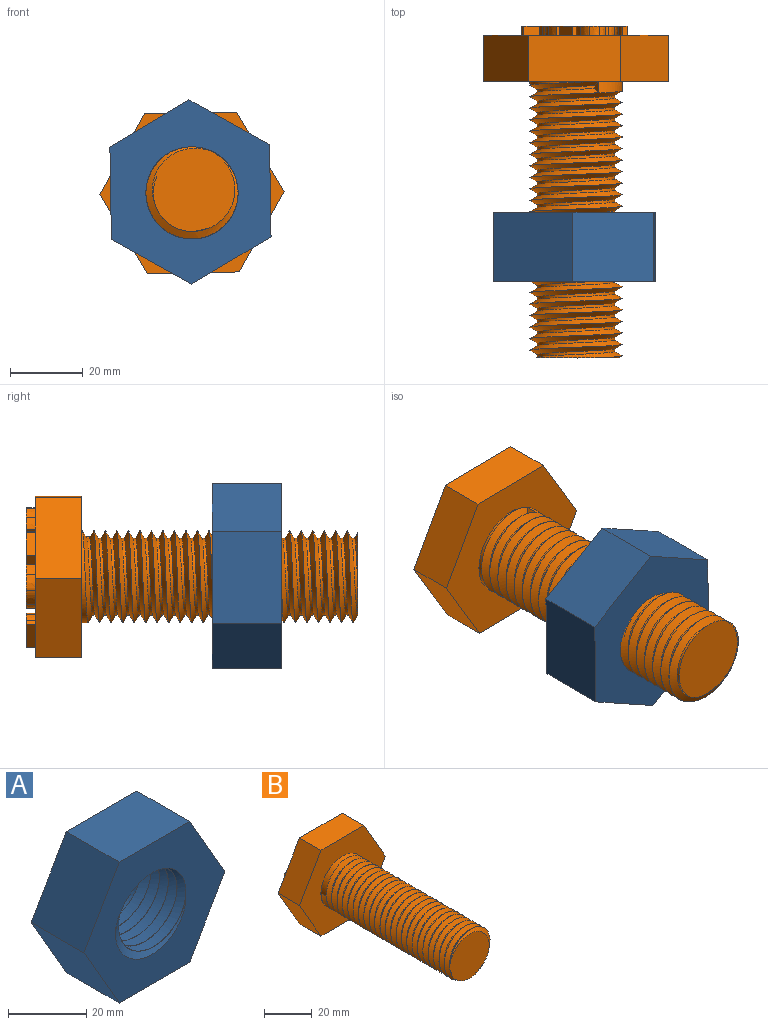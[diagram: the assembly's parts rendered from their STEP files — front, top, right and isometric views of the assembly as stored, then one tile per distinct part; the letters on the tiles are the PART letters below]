
ASSEMBLY  parts=2 mates=1
PART A: 12 faces, bbox 53x23.4x46.2 mm
  f0: cylinder r=11.33mm len=22.66mm, axis (0,1,0), area 111.2mm2, adj f1,f8,f9,f10,f11
  f1: plane 53.04x46.23mm, normal (0,-1,0), area 1167.7mm2, adj f0,f2,f3,f4,f5,f6,f7,f10
  f2: plane 22x19.05mm, normal (0.87,0,0.5), area 483.9mm2, adj f1,f3,f7,f8
  f3: plane 25.4x19.05mm, normal (0,0,1), area 483.9mm2, adj f1,f2,f4,f8
  f4: plane 22x19.05mm, normal (-0.87,0,0.5), area 483.9mm2, adj f1,f3,f5,f8
  f5: plane 22x19.05mm, normal (-0.87,0,-0.5), area 483.9mm2, adj f1,f4,f6,f8
  f6: plane 25.4x19.05mm, normal (0,0,-1), area 483.9mm2, adj f1,f5,f7,f8
  f7: plane 22x19.05mm, normal (0.87,0,-0.5), area 483.9mm2, adj f1,f2,f6,f8
  f8: plane 50.8x43.99mm, normal (0,1,0), area 1273mm2, adj f0,f2,f3,f4,f5,f6,f7
  f9: plane 3.17x2.74mm, normal (0,0,1), area 4.3mm2, adj f0,f10,f11
  f10: bspline ~32.5x28.14mm, area 1450.3mm2, adj f0,f1,f9,f11
  f11: bspline ~32.5x28.14mm, area 1329.5mm2, adj f0,f1,f9,f10
PART B: 80 faces, bbox 52.1x94.3x45.3 mm
  f0: plane 22x12.7mm, normal (0.87,0,0.5), area 322.6mm2, adj f1,f5,f6,f7
  f1: plane 25.4x12.7mm, normal (0,0,1), area 322.6mm2, adj f0,f2,f6,f7
  f2: plane 22x12.7mm, normal (-0.87,0,0.5), area 322.6mm2, adj f1,f3,f6,f7
  f3: plane 22x12.7mm, normal (-0.87,0,-0.5), area 322.6mm2, adj f2,f4,f6,f7
  f4: plane 25.4x12.7mm, normal (0,0,-1), area 322.6mm2, adj f3,f5,f6,f7
  f5: plane 22x12.7mm, normal (0.87,0,-0.5), area 322.6mm2, adj f0,f4,f6,f7
  f6: plane 50.8x43.99mm, normal (0,-1,0), area 1169.5mm2, adj f0,f1,f2,f3,f4,f5,f8
  f7: plane 50.8x43.99mm, normal (0,1,0), area 1514mm2, adj f0,f1,f2,f3,f4,f5,f14,f15
  f8: cylinder r=12.7mm len=76.2mm, axis (0,1,0), area 340.6mm2, adj f6,f9,f10,f11,f13
  f9: plane 24.64x24.04mm, normal (0,-1,0), area 411mm2, adj f8,f11,f12,f13
  f10: plane 3.17x2.06mm, normal (0,0,-1), area 4.1mm2, adj f8,f11,f12,f13
  f11: bspline ~75.8x29.33mm, area 4036.3mm2, adj f8,f9,f10,f12
  f12: cylinder r=10.64mm len=75.01mm, axis (0,1,0), area 699.9mm2, adj f9,f10,f11,f13
  f13: bspline ~77.39x29.33mm, area 4156.1mm2, adj f8,f9,f10,f12
  f14: extruded ~4.77x3.7mm, area 17.5mm2, adj f7,f15,f28,f29
  f15: plane 3.3x2.54mm, normal (0,0,1), area 8.4mm2, adj f7,f14,f16,f29
  f16: plane 12.72x2.54mm, normal (1,0,0), area 32.3mm2, adj f7,f15,f17,f29
  f17: plane 2.54x1.48mm, normal (0,0,-1), area 3.8mm2, adj f7,f16,f18,f29
  f18: plane 5x2.54mm, normal (-1,0,0), area 12.7mm2, adj f7,f17,f19,f29
  f19: plane 2.54x1.5mm, normal (0,0,-1), area 3.8mm2, adj f7,f18,f20,f29
  f20: extruded ~3.77x2.54mm, area 10.1mm2, adj f7,f19,f28,f29
  f21: plane 5.17x2.54mm, normal (-1,0,0), area 13.1mm2, adj f22,f27,f29,f30
  f22: plane 2.54x1.65mm, normal (0,0,-1), area 4.2mm2, adj f21,f23,f29,f30
  f23: extruded ~2.57x2.54mm, area 6.8mm2, adj f22,f24,f29,f30
  f24: extruded ~2.54x1.88mm, area 5.4mm2, adj f23,f25,f29,f30
  f25: extruded ~2.54x2.04mm, area 5.9mm2, adj f24,f26,f29,f30
  f26: extruded ~2.84x2.54mm, area 7.5mm2, adj f25,f27,f29,f30
  f27: plane 2.54x1.33mm, normal (0,0,1), area 3.4mm2, adj f21,f26,f29,f30
  f28: extruded ~2.97x2.54mm, area 8.6mm2, adj f7,f14,f20,f29
  f29: plane 12.72x8.06mm, normal (0,1,0), area 39.9mm2, adj f14,f15,f16,f17,f18,f19,f20,f21
  f30: plane 5.17x5.05mm, normal (0,1,0), area 23.2mm2, adj f21,f22,f23,f24,f25,f26,f27
  f31: extruded ~2.89x2.54mm, area 7.6mm2, adj f7,f32,f45,f46
  f32: plane 2.54x1.27mm, normal (-0.9,0,-0.44), area 3.6mm2, adj f7,f31,f33,f46
  f33: extruded ~3.5x2.54mm, area 9.1mm2, adj f7,f32,f34,f46
  f34: extruded ~3.27x2.54mm, area 8.6mm2, adj f7,f33,f35,f46
  f35: extruded ~2.54x2.28mm, area 8mm2, adj f7,f34,f36,f46
  f36: extruded ~3.44x2.54mm, area 9mm2, adj f7,f35,f37,f46
  f37: extruded ~4.85x2.54mm, area 13.2mm2, adj f7,f36,f38,f46
  f38: extruded ~4.34x2.54mm, area 12.2mm2, adj f7,f37,f39,f46
  f39: extruded ~3.26x2.54mm, area 8.4mm2, adj f7,f38,f40,f46
  f40: plane 2.54x1.29mm, normal (-1,0,0), area 3.3mm2, adj f7,f39,f41,f46
  f41: extruded ~3.04x2.54mm, area 7.8mm2, adj f7,f40,f42,f46
  f42: extruded ~3.34x2.54mm, area 9.5mm2, adj f7,f41,f43,f46
  f43: extruded ~3.86x2.54mm, area 10.5mm2, adj f7,f42,f44,f46
  f44: extruded ~3.82x2.54mm, area 10.4mm2, adj f7,f43,f45,f46
  f45: extruded ~3.31x2.54mm, area 9.4mm2, adj f7,f31,f44,f46
  f46: plane 13.07x9.62mm, normal (0,1,0), area 35.4mm2, adj f31,f32,f33,f34,f35,f36,f37,f38
  f47: plane 7.09x2.54mm, normal (0,0,-1), area 18mm2, adj f7,f48,f52,f53
  f48: plane 2.54x1.34mm, normal (-1,0,0), area 3.4mm2, adj f7,f47,f49,f53
  f49: plane 5.61x2.54mm, normal (0,0,1), area 14.3mm2, adj f7,f48,f50,f53
  f50: plane 11.38x2.54mm, normal (-1,0,0), area 28.9mm2, adj f7,f49,f51,f53
  f51: plane 2.54x1.48mm, normal (0,0,1), area 3.8mm2, adj f7,f50,f52,f53
  f52: plane 12.72x2.54mm, normal (1,0,0), area 32.3mm2, adj f7,f47,f51,f53
  f53: plane 12.72x7.09mm, normal (0,1,0), area 26.3mm2, adj f47,f48,f49,f50,f51,f52
  f54: extruded ~2.54x2.12mm, area 5.9mm2, adj f7,f55,f78,f79
  f55: extruded ~2.75x2.54mm, area 8.1mm2, adj f7,f54,f56,f79
  f56: extruded ~2.54x1.77mm, area 4.9mm2, adj f7,f55,f57,f79
  f57: extruded ~2.54x0.82mm, area 2.9mm2, adj f7,f56,f58,f79
  f58: extruded ~2.54x1.08mm, area 2.9mm2, adj f7,f57,f59,f79
  f59: extruded ~2.54x1.4mm, area 4.1mm2, adj f7,f58,f60,f79
  f60: extruded ~2.54x1.84mm, area 4.9mm2, adj f7,f59,f61,f79
  f61: extruded ~3.06x2.54mm, area 8mm2, adj f7,f60,f62,f79
  f62: plane 2.54x1.29mm, normal (-0.94,0,-0.34), area 3.5mm2, adj f7,f61,f63,f79
  f63: extruded ~3.49x2.54mm, area 9.1mm2, adj f7,f62,f64,f79
  f64: extruded ~2.92x2.54mm, area 7.9mm2, adj f7,f63,f65,f79
  f65: extruded ~2.54x2.34mm, area 6.8mm2, adj f7,f64,f66,f79
  f66: extruded ~2.54x2.27mm, area 6.2mm2, adj f7,f65,f67,f79
  f67: extruded ~2.54x2.53mm, area 7.6mm2, adj f7,f66,f68,f79
  f68: extruded ~2.54x1.89mm, area 5.2mm2, adj f7,f67,f69,f79
  f69: extruded ~2.54x0.89mm, area 3mm2, adj f7,f68,f70,f79
  f70: extruded ~2.54x1.08mm, area 2.9mm2, adj f7,f69,f71,f79
  f71: extruded ~2.54x1.56mm, area 4.6mm2, adj f7,f70,f72,f79
  f72: extruded ~2.54x2.23mm, area 5.9mm2, adj f7,f71,f73,f79
  f73: extruded ~2.54x1.83mm, area 4.7mm2, adj f7,f72,f74,f79
  f74: extruded ~2.54x1.71mm, area 4.5mm2, adj f7,f73,f75,f79
  f75: plane 2.54x1.43mm, normal (1,0,0), area 3.6mm2, adj f7,f74,f76,f79
  f76: extruded ~3.48x2.54mm, area 9mm2, adj f7,f75,f77,f79
  f77: extruded ~3.31x2.54mm, area 8.9mm2, adj f7,f76,f78,f79
  f78: extruded ~2.62x2.54mm, area 7.6mm2, adj f7,f54,f77,f79
  f79: plane 13.07x8mm, normal (0,1,0), area 37.4mm2, adj f54,f55,f56,f57,f58,f59,f60,f61
PLACE A rot(axis=(-0.97,0,0.25),180deg) t=(90.69,-254.06,61.07)mm
PLACE B rot(axis=(0,1,0),119.1deg) t=(91.11,-135.47,60.83)mm
MATE cylindrical A.f1 <-> B.f8  axis (0,1,0) through (91.11,-184.21,60.83)mm
